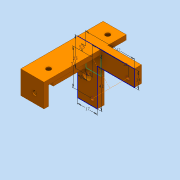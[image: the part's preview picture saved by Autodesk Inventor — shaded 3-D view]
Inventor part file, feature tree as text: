
AUTODESK INVENTOR PART (.ipt)
format: ipt  version: 2016 (Build 200138000, 138)  size: 243,712 bytes
history: native  units: mm
features: extrude x10, sketch x10, hole x7
ambient origin geometry x8: Origin, YZ Plane, XZ Plane, XY Plane, X Axis, Y Axis, Z Axis, Center Point
bodies: Solid1 (feature_tree)
feature tree (27):
  extrude  "Extrusion1"  Depth=20.0mm
  extrude  "Extrusion2"  Depth=45.0mm TaperAngle=0.0deg
  hole  "Hole2"  [1 undecoded]
  hole  "Hole3"  [1 undecoded]
  hole  "Hole4"  [1 undecoded]
  sketch  "Sketch3"  dims[d15=37.0mm d16=8.0mm d17=4.0mm d18=6.0mm d19=8.0mm d20=2.0mm d21=90.0deg d22=8.0mm d23=20.594885mm]
  sketch  "Sketch4"  dims[d24=37.0mm d25=8.0mm d26=4.0mm d27=6.0mm d28=8.0mm d29=2.0mm d30=90.0deg d31=8.0mm d32=20.594885mm]
  sketch  "Sketch5"  dims[d33=8.0mm d34=8.0mm d35=4.0mm d36=6.0mm d37=8.0mm d38=2.0mm d39=90.0deg d40=8.0mm d41=20.594885mm d51=7.0mm]
  extrude  "Extrusion3"  Depth=17.0mm
  extrude  "Extrusion4"  Depth=42.0mm
  extrude  "Extrusion5"  Depth=5.5mm
  sketch  "Sketch6"  dims[d52=7.0mm d53=7.0mm]
  extrude  "Extrusion6"  Depth=10.0mm
  hole  "Hole5"  [1 undecoded]
  extrude  "Extrusion7"  Depth=14.0mm
  hole  "Hole6"  [1 undecoded]
  hole  "Hole7"  [1 undecoded]
  sketch  "Sketch8"  dims[d58=3.2mm d59=0.0mm d62=17.0mm]
  extrude  "Extrusion8"  Depth=4.0mm
  extrude  "Extrusion9"  Depth=4.0mm
  hole  "Hole8"  [1 undecoded]
  extrude  "Extrusion10"  Depth=16.0mm TaperAngle=0.0deg
  sketch  "Sketch1"  dims[d0=20.0mm d1=20.0mm]
  sketch  "Sketch2"  dims[d2=4.0mm d3=0.0mm d4=45.0mm d5=0.0mm]
  sketch  "Sketch7"  dims[d54=3.2mm d55=0.0mm d56=3.2mm d57=0.0mm]
  sketch  "Sketch9"  dims[d65=42.0mm d66=42.0mm]
  sketch  "Sketch11"  dims[d68=5.5mm d69=5.5mm d70=31.0mm d71=31.0mm d72=14.0mm d73=6.0mm d74=0.0mm d75=3.0mm d76=6.0mm d77=4.0mm d78=2.0mm d79=90.0deg d80=8.0mm d81=20.594885mm d82=20.0mm d83=4.0mm d84=4.0mm d85=20.0mm d86=16.0mm d87=0.0mm d88=8.0mm d89=8.0mm d90=4.0mm d91=6.0mm d92=4.0mm d93=2.0mm d94=90.0deg d95=8.0mm d96=20.594885mm d97=8.0mm d98=8.0mm d99=4.0mm d100=6.0mm d101=4.0mm d102=2.0mm d103=90.0deg d104=8.0mm d105=20.594885mm d106=7.0mm d107=7.0mm d108=3.2mm d109=0.0mm d110=3.2mm d111=0.0mm d112=8.0mm d113=25.0mm d114=8.0mm d115=6.0mm d116=4.0mm d117=2.0mm d118=90.0deg d119=8.0mm d120=20.594885mm d121=8.0mm d122=25.0mm d123=7.0mm d127=10.0mm d128=0.0mm]
note: 7 required parameter values undecoded (feature->parameter linkage not recoverable at this tier; creation-order binding heuristic only, values carry confidence <= 0.55)
